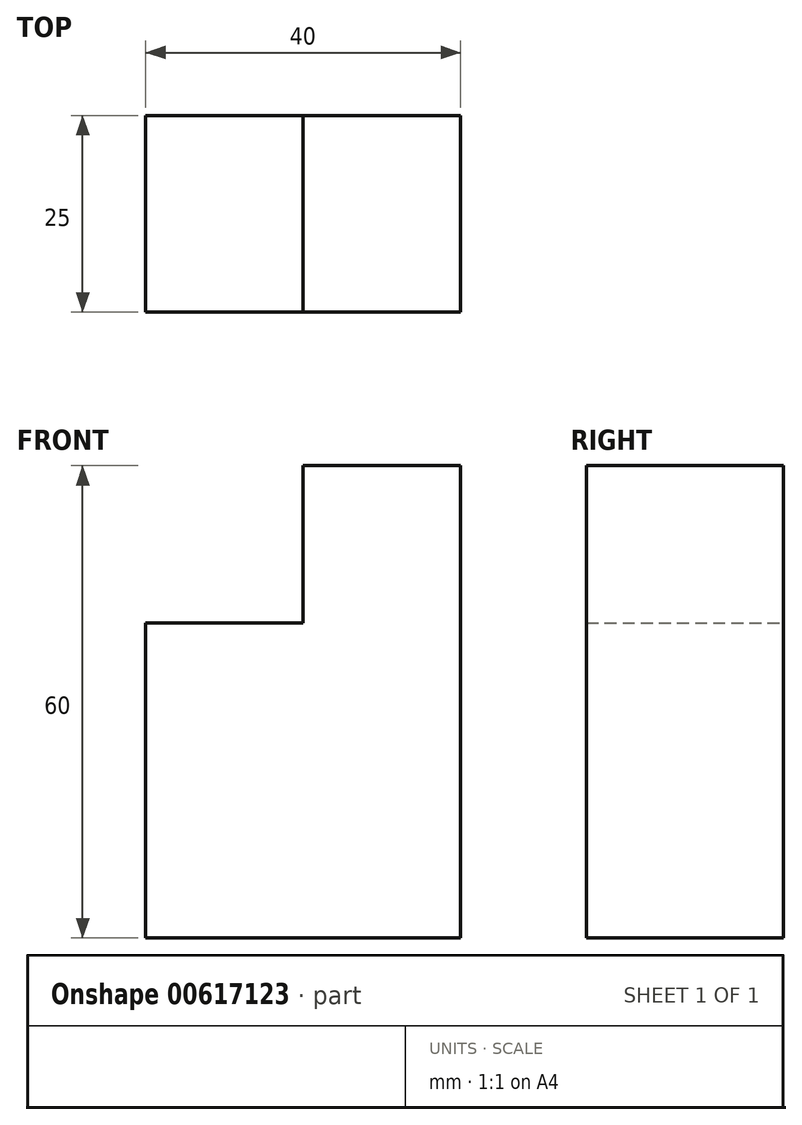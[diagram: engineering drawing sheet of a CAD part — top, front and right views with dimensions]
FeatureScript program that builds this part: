
annotation { "Feature Type Name" : "Feature", "Feature Type Description" : "" }
export const myFeature = defineFeature(function(context is Context, id is Id, definition is map)
    precondition{}
    {
        {
            var Q0;
            Q0=qCreatedBy(makeId("Front.planeOp"),FACE);
            var sketch = newSketch(context, id + "F0", { "sketchPlane" : qUnion([Q0])});
            skLineSegment(sketch, "E0", {"start": v(-20, 16.3) * mm, "end": v(0, 16.3) * mm});
            skLineSegment(sketch, "E1", {"start": v(0, 16.3) * mm, "end": v(0, 36.3) * mm});
            skLineSegment(sketch, "E2", {"start": v(0, 36.3) * mm, "end": v(20, 36.3) * mm});
            skLineSegment(sketch, "E3", {"start": v(20, 36.3) * mm, "end": v(20, -23.7) * mm});
            skLineSegment(sketch, "E4", {"start": v(20, -23.7) * mm, "end": v(-20, -23.7) * mm});
            skLineSegment(sketch, "E5", {"start": v(-20, -23.7) * mm, "end": v(-20, 16.3) * mm});
            skSolve(sketch);
        }
        {
            var Q0;
            Q0 = qSketchRegion(id + "F0", true);
            extrude(context, id + "F1", {"entities" : qUnion([Q0]), "depth" : 25 * mm, "offsetDistance" : 25 * mm});
        }
    });
